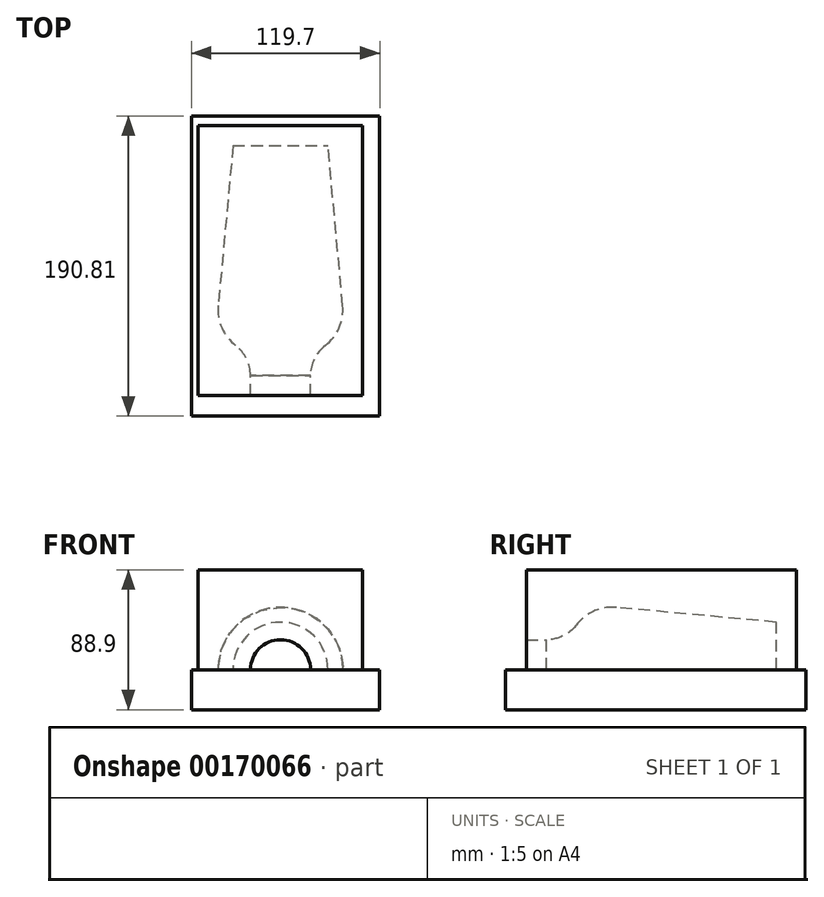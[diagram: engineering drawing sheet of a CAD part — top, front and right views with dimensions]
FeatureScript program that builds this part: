
annotation { "Feature Type Name" : "Feature", "Feature Type Description" : "" }
export const myFeature = defineFeature(function(context is Context, id is Id, definition is map)
    precondition{}
    {
        {
            var Q0;
            Q0=qCreatedBy(makeId("Right.planeOp"),FACE);
            var sketch = newSketch(context, id + "F0", { "sketchPlane" : qUnion([Q0])});
            skLineSegment(sketch, "E0", {"start": v(0, 0) * mm, "end": v(0, 43.66) * mm, "construction": true});
            skLineSegment(sketch, "E1", {"start": v(0, 43.66) * mm, "end": v(146.05, 30.16) * mm, "construction": true});
            skLineSegment(sketch, "E2", {"start": v(146.05, 30.16) * mm, "end": v(146.05, 0) * mm, "construction": true});
            skLineSegment(sketch, "E3", {"start": v(146.05, 0) * mm, "end": v(0, 0) * mm, "construction": true});
            skPoint(sketch, "E4", {"position": v(0, 19.05) * mm});
            skArc(sketch, "E5", {"start": v(0, 19.05) * mm, "mid": v(10.62, 21.53) * mm, "end": v(19.05, 28.45) * mm});
            skArc(sketch, "E6", {"start": v(44.45, 39.55) * mm, "mid": v(30.32, 37.27) * mm, "end": v(19.05, 28.45) * mm});
            skLineSegment(sketch, "E7", {"start": v(0, 19.05) * mm, "end": v(146.05, 19.05) * mm, "construction": true});
            skPoint(sketch, "E7.endSnap0", {"position": v(146.05, 15.08) * mm});
            skLineSegment(sketch, "E8", {"start": v(44.45, 39.55) * mm, "end": v(146.05, 30.16) * mm});
            skLineSegment(sketch, "E9", {"start": v(146.05, 0) * mm, "end": v(146.05, 30.16) * mm});
            skLineSegment(sketch, "E10", {"start": v(0, 19.05) * mm, "end": v(0, 0) * mm});
            skLineSegment(sketch, "E11", {"start": v(146.05, 0) * mm, "end": v(0, 0) * mm});
            skSolve(sketch);
        }
        {
            var Q0;
            Q0 = qSketchRegion(id + "F0", true);
            var Q1;
            Q1=sQuery(id+"F0.wireOp",EDGE,"E3");
            revolve(context, id + "F1", {"entities" : qUnion([Q0]), "axis" : qUnion([Q1]), "revolveType" : RevolveType.FULL});
        }
        {
            var Q0;
            Q0=qCreatedBy(makeId("Top.planeOp"),FACE);
            var sketch = newSketch(context, id + "F2", { "sketchPlane" : qUnion([Q0])});
            skLineSegment(sketch, "E12.bottom", {"start": v(-49.06, -9.9) * mm, "end": v(48.42, -9.9) * mm});
            skLineSegment(sketch, "E12.top", {"start": v(-49.06, 160.68) * mm, "end": v(48.42, 160.68) * mm});
            skLineSegment(sketch, "E12.left", {"start": v(-49.06, -9.9) * mm, "end": v(-49.06, 160.68) * mm});
            skLineSegment(sketch, "E12.right", {"start": v(48.42, -9.9) * mm, "end": v(48.42, 160.68) * mm});
            skSolve(sketch);
        }
        {
            var Q0;
            Q0 = qSketchRegion(id + "F2", true);
            extrude(context, id + "F3", {"entities" : qUnion([Q0]), "operationType" : NewBodyOperationType.REMOVE, "endBound" : BoundingType.THROUGH_ALL, "oppositeDirection" : true, "depth" : 25.4 * mm});
        }
        {
            var Q0;
            Q0=makeQuery(id+"F3.boolean.opBoolean","COPY",FACE,{"derivedFrom":makeQuery(id+"F3.opExtrude","CAP_FACE",FACE,{"disambiguationData":[OSD([sQuery(id+"F2.wireOp",EDGE,"E12.bottom"),sQuery(id+"F2.wireOp",EDGE,"E12.top"),sQuery(id+"F2.wireOp",EDGE,"E12.left"),sQuery(id+"F2.wireOp",EDGE,"E12.right")])],"isStart":true})});
            var sketch = newSketch(context, id + "F4", { "sketchPlane" : qUnion([Q0])});
            skLineSegment(sketch, "E13.bottom", {"start": v(63.05, 25.83) * mm, "end": v(-56.65, 25.83) * mm});
            skLineSegment(sketch, "E13.top", {"start": v(63.05, -164.98) * mm, "end": v(-56.65, -164.98) * mm});
            skLineSegment(sketch, "E13.left", {"start": v(63.05, 25.83) * mm, "end": v(63.05, -164.98) * mm});
            skLineSegment(sketch, "E13.right", {"start": v(-56.65, 25.83) * mm, "end": v(-56.65, -164.98) * mm});
            skSolve(sketch);
        }
        {
            var Q0;
            Q0 = qSketchRegion(id + "F4", true);
            extrude(context, id + "F5", {"entities" : qUnion([Q0]), "operationType" : NewBodyOperationType.ADD, "depth" : 25.4 * mm});
        }
        {
            var Q0;
            Q0=qCreatedBy(makeId("Top.planeOp"),FACE);
            cPlane(context, id + "F6", {"entities" : qUnion([Q0]), "cplaneType" : CPlaneType.OFFSET, "offset" : 63.5 * mm, "width" : 152.4 * mm, "height" : 152.4 * mm});
        }
        {
            var Q0;
            Q0=qCreatedBy(id+"F6.planeOp",FACE);
            var sketch = newSketch(context, id + "F7", { "sketchPlane" : qUnion([Q0])});
            skLineSegment(sketch, "E14.bottom", {"start": v(-52.25, -12.7) * mm, "end": v(52.25, -12.7) * mm});
            skLineSegment(sketch, "E14.top", {"start": v(-52.25, 158.75) * mm, "end": v(52.25, 158.75) * mm});
            skLineSegment(sketch, "E14.left", {"start": v(-52.25, -12.7) * mm, "end": v(-52.25, 158.75) * mm});
            skLineSegment(sketch, "E14.right", {"start": v(52.25, -12.7) * mm, "end": v(52.25, 158.75) * mm});
            skSolve(sketch);
        }
        {
            var Q0;
            Q0=makeQuery(id+"F7.imprint","IMPRINT",FACE,{"disambiguationData":[TD([[makeQuery(id+"F7.imprint","IMPRINT",EDGE,{"derivedFrom":sQuery(id+"F7.wireOp",EDGE,"E14.bottom")}),1.0]])]});
            extrude(context, id + "F8", {"entities" : qUnion([Q0]), "endBound" : BoundingType.UP_TO_NEXT, "oppositeDirection" : true, "depth" : 25.4 * mm});
        }
        {
            var Q0;
            Q0=makeQuery(id+"F8.opExtrude","CAP_FACE",FACE,{"disambiguationData":[OSD([sQuery(id+"F7.wireOp",EDGE,"E14.bottom"),sQuery(id+"F7.wireOp",EDGE,"E14.top"),sQuery(id+"F7.wireOp",EDGE,"E14.left"),sQuery(id+"F7.wireOp",EDGE,"E14.right")]),topologyDisambiguationEdgeConnected([makeQuery(id+"F1.opRevolve","SWEPT_FACE",FACE,{"disambiguationData":[OSD([sQuery(id+"F0.wireOp",EDGE,"E10")])]})])],"isStart":false});
            var sketch = newSketch(context, id + "F9", { "sketchPlane" : qUnion([Q0])});
            skArc(sketch, "E15.0", {"start": v(19.05, 0) * mm, "mid": v(0, 19.05) * mm, "end": v(-19.05, 0) * mm});
            skLineSegment(sketch, "E15.1", {"start": v(-19.05, 0) * mm, "end": v(19.05, 0) * mm});
            skSolve(sketch);
        }
        {
            var Q0;
            Q0 = qSketchRegion(id + "F9", true);
            extrude(context, id + "F10", {"entities" : qUnion([Q0]), "operationType" : NewBodyOperationType.REMOVE, "oppositeDirection" : true, "depth" : 25.4 * mm});
        }
    });
